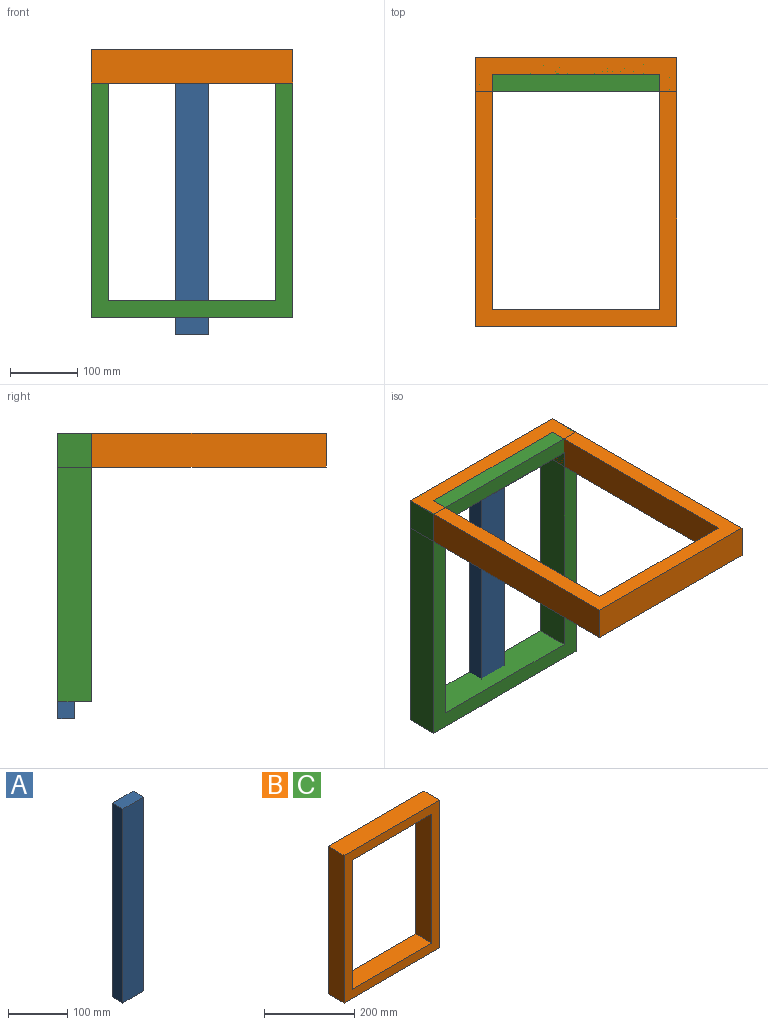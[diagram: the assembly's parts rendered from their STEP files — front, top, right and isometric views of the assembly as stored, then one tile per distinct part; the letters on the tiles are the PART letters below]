
ASSEMBLY  parts=3 mates=2
PART A: 6 faces, bbox 50x25x400 mm
  f0: plane 400x25mm, normal (1,0,0), area 10000mm2, adj f1,f3,f4,f5
  f1: plane 50x25mm, normal (0,0,1), area 1250mm2, adj f0,f2,f4,f5
  f2: plane 400x25mm, normal (-1,0,0), area 10000mm2, adj f1,f3,f4,f5
  f3: plane 50x25mm, normal (0,0,-1), area 1250mm2, adj f0,f2,f4,f5
  f4: plane 400x50mm, normal (0,-1,0), area 20000mm2, adj f0,f1,f2,f3
  f5: plane 400x50mm, normal (0,1,0), area 20000mm2, adj f0,f1,f2,f3
PART B: 10 faces, bbox 300x50x400 mm
  f0: plane 400x300mm, normal (0,-1,0), area 32500mm2, adj f2,f3,f4,f5,f6,f7,f8,f9
  f1: plane 400x300mm, normal (0,1,0), area 32500mm2, adj f2,f3,f4,f5,f6,f7,f8,f9
  f2: plane 400x50mm, normal (1,0,0), area 20000mm2, adj f0,f1,f3,f5
  f3: plane 300x50mm, normal (0,0,1), area 15000mm2, adj f0,f1,f2,f4
  f4: plane 400x50mm, normal (-1,0,0), area 20000mm2, adj f0,f1,f3,f5
  f5: plane 300x50mm, normal (0,0,-1), area 15000mm2, adj f0,f1,f2,f4
  f6: plane 250x50mm, normal (0,0,1), area 12500mm2, adj f0,f1,f7,f9
  f7: plane 350x50mm, normal (-1,0,0), area 17500mm2, adj f0,f1,f6,f8
  f8: plane 250x50mm, normal (0,0,-1), area 12500mm2, adj f0,f1,f7,f9
  f9: plane 350x50mm, normal (1,0,0), area 17500mm2, adj f0,f1,f6,f8
PART C: same geometry as B
PLACE A t=(107.39,-361.97,140.69)mm
PLACE B rot(axis=(-1,0,0),90deg) t=(107.39,-561.97,315.69)mm
PLACE C t=(107.39,-361.97,165.69)mm
MATE fastened A.f5 <-> B.f3  axis (0,1,0) through (107.39,-361.97,340.69)mm
MATE fastened B.f3 <-> C.f1  axis (0,1,0) through (107.39,-361.97,340.69)mm
